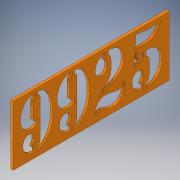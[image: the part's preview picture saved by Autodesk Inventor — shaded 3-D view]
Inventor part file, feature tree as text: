
AUTODESK INVENTOR PART (.ipt)
format: ipt  version: 2019 (Build 230136000, 136)  size: 464,384 bytes
history: native  units: in
note: dims shown in document units (in); Inventor stores cm internally (conversion verified against a paired STEP export)
features: extrude x2, thicken_offset x2, sketch x2, projected_geometry x1
ambient origin geometry x8: Origin, YZ Plane, XZ Plane, XY Plane, X Axis, Y Axis, Z Axis, Center Point
bodies: Solid1 (feature_tree)
feature tree (7):
  extrude  "Extrusion1"  Depth=8.5in
  extrude  "Extrusion3"  Depth=0.25in TaperAngle=0.0deg
  thicken_offset  "Thicken1"
  thicken_offset  "Thicken2"
  sketch  "Sketch1"  dims[d0=3.0in d1=8.5in]
  sketch  "Sketch2"  dims[d2=0.125in d3=0.0in d9=0.25in d10=0.0in d13=0.35in d14=0.35in d15=0.35in d16=0.35in]
  projected_geometry  "Projected Loop1"
